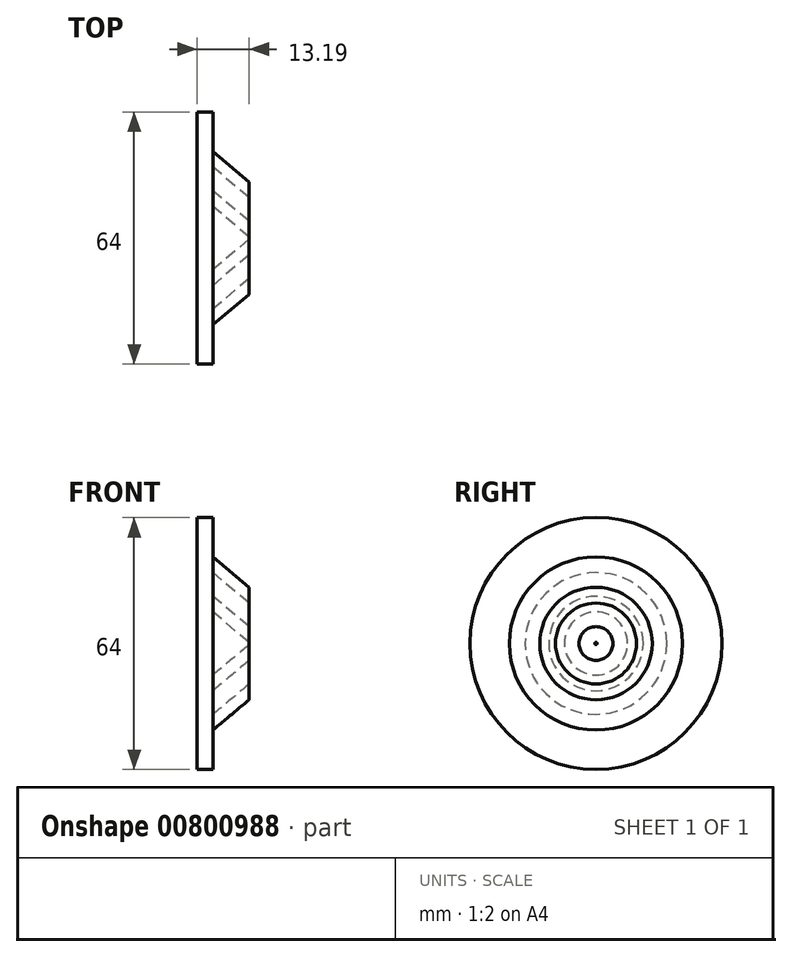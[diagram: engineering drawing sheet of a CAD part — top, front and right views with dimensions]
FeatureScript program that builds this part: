
annotation { "Feature Type Name" : "Feature", "Feature Type Description" : "" }
export const myFeature = defineFeature(function(context is Context, id is Id, definition is map)
    precondition{}
    {
        {
            var Q0;
            Q0=qCreatedBy(makeId("Top.planeOp"),FACE);
            var sketch = newSketch(context, id + "F0", { "sketchPlane" : qUnion([Q0])});
            skLineSegment(sketch, "E0", {"start": v(0, 0) * mm, "end": v(0, -32) * mm});
            skLineSegment(sketch, "E1", {"start": v(0, -32) * mm, "end": v(4, -32) * mm});
            skLineSegment(sketch, "E2", {"start": v(4, -32) * mm, "end": v(4, -22) * mm});
            skLineSegment(sketch, "E3", {"start": v(4, -22) * mm, "end": v(13.2, -14.29) * mm});
            skLineSegment(sketch, "E4", {"start": v(13.2, -14.29) * mm, "end": v(13.2, -10.29) * mm});
            skLineSegment(sketch, "E5", {"start": v(13.2, -10.29) * mm, "end": v(4, -18) * mm});
            skLineSegment(sketch, "E6", {"start": v(4, -18) * mm, "end": v(4, -12) * mm});
            skLineSegment(sketch, "E7", {"start": v(4, -12) * mm, "end": v(13.2, -4.29) * mm});
            skLineSegment(sketch, "E8", {"start": v(4, -8) * mm, "end": v(4, 0) * mm});
            skLineSegment(sketch, "E9", {"start": v(4, 0) * mm, "end": v(0, 0) * mm});
            skLineSegment(sketch, "E10", {"start": v(13.2, -4.29) * mm, "end": v(13.2, -0.29) * mm});
            skLineSegment(sketch, "E11", {"start": v(13.2, -0.29) * mm, "end": v(4, -8) * mm});
            skSolve(sketch);
        }
        {
            var Q0;
            Q0=makeQuery(id+"F0.imprint","IMPRINT",FACE,{"disambiguationData":[TD([[makeQuery(id+"F0.imprint","IMPRINT",EDGE,{"derivedFrom":sQuery(id+"F0.wireOp",EDGE,"E0")}),1.0]])]});
            var Q1;
            Q1=sQuery(id+"F0.wireOp",EDGE,"E9");
            revolve(context, id + "F1", {"surfaceOperationType" : NewSurfaceOperationType.NEW, "entities" : qUnion([Q0]), "axis" : qUnion([Q1]), "revolveType" : RevolveType.FULL});
        }
    });
